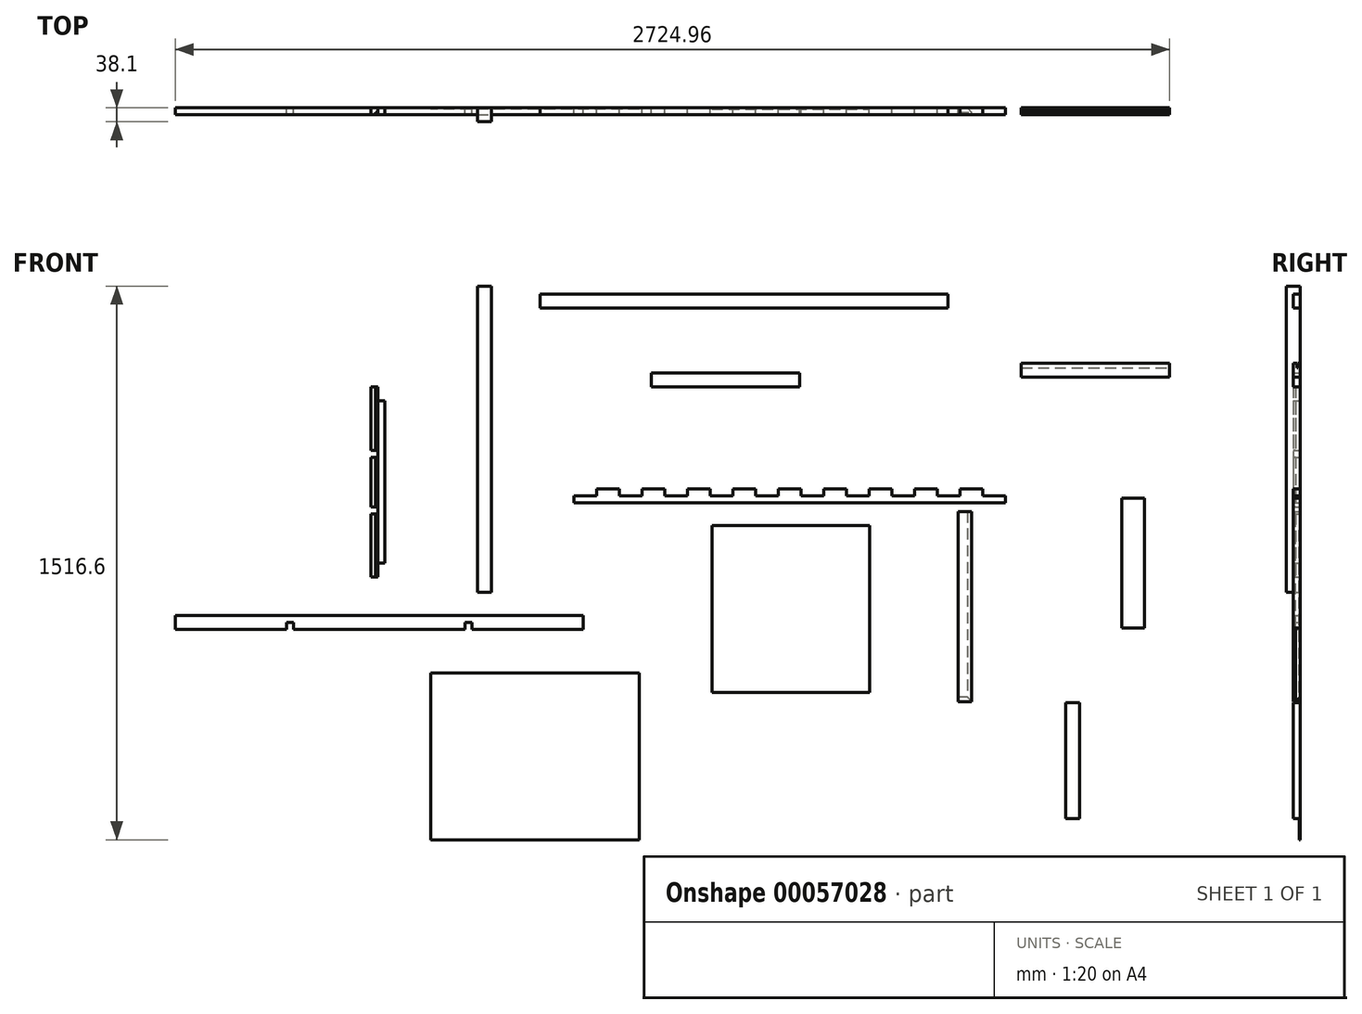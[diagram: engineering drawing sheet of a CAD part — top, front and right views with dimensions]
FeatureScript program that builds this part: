
annotation { "Feature Type Name" : "Feature", "Feature Type Description" : "" }
export const myFeature = defineFeature(function(context is Context, id is Id, definition is map)
    precondition{}
    {
        {
            var Q0;
            Q0=qCreatedBy(makeId("Front.planeOp"),FACE);
            var sketch = newSketch(context, id + "F0", { "sketchPlane" : qUnion([Q0])});
            skLineSegment(sketch, "E0.bottom", {"start": v(-712.43, -105.84) * mm, "end": v(-650.2, -105.84) * mm});
            skLineSegment(sketch, "E0.left", {"start": v(-774.66, -124.9) * mm, "end": v(-774.66, -143.94) * mm});
            skPoint(sketch, "E1.oppositeSnap0", {"position": v(-876.9, -124.9) * mm});
            skLineSegment(sketch, "E1.top", {"start": v(-774.66, -124.9) * mm, "end": v(-712.43, -124.9) * mm});
            skLineSegment(sketch, "E1.right", {"start": v(-712.43, -105.84) * mm, "end": v(-712.43, -124.9) * mm});
            skLineSegment(sketch, "E2.top", {"start": v(-650.2, -124.9) * mm, "end": v(-587.97, -124.9) * mm});
            skLineSegment(sketch, "E2.left", {"start": v(-650.2, -105.84) * mm, "end": v(-650.2, -124.9) * mm});
            skLineSegment(sketch, "E2.right", {"start": v(-587.97, -105.84) * mm, "end": v(-587.97, -124.9) * mm});
            skLineSegment(sketch, "E3.top", {"start": v(-525.74, -124.9) * mm, "end": v(-463.51, -124.9) * mm});
            skLineSegment(sketch, "E3.left", {"start": v(-525.74, -105.84) * mm, "end": v(-525.74, -124.9) * mm});
            skLineSegment(sketch, "E3.right", {"start": v(-463.51, -105.84) * mm, "end": v(-463.51, -124.9) * mm});
            skLineSegment(sketch, "E4.top", {"start": v(-401.28, -124.9) * mm, "end": v(-339.05, -124.9) * mm});
            skLineSegment(sketch, "E4.left", {"start": v(-401.28, -105.84) * mm, "end": v(-401.28, -124.9) * mm});
            skLineSegment(sketch, "E4.right", {"start": v(-339.05, -105.84) * mm, "end": v(-339.05, -124.9) * mm});
            skLineSegment(sketch, "E5.top", {"start": v(-276.82, -124.9) * mm, "end": v(-214.6, -124.9) * mm});
            skLineSegment(sketch, "E5.left", {"start": v(-276.82, -105.84) * mm, "end": v(-276.82, -124.9) * mm});
            skLineSegment(sketch, "E5.right", {"start": v(-214.6, -105.84) * mm, "end": v(-214.6, -124.9) * mm});
            skLineSegment(sketch, "E6.top", {"start": v(-152.36, -124.9) * mm, "end": v(-90.13, -124.9) * mm});
            skLineSegment(sketch, "E6.left", {"start": v(-152.36, -105.84) * mm, "end": v(-152.36, -124.9) * mm});
            skLineSegment(sketch, "E6.right", {"start": v(-90.13, -105.84) * mm, "end": v(-90.13, -124.9) * mm});
            skLineSegment(sketch, "E7.top", {"start": v(-27.9, -124.9) * mm, "end": v(34.33, -124.9) * mm});
            skLineSegment(sketch, "E7.left", {"start": v(-27.9, -105.84) * mm, "end": v(-27.9, -124.9) * mm});
            skLineSegment(sketch, "E7.right", {"start": v(34.33, -105.84) * mm, "end": v(34.33, -124.9) * mm});
            skLineSegment(sketch, "E8.top", {"start": v(96.56, -124.9) * mm, "end": v(158.79, -124.9) * mm});
            skLineSegment(sketch, "E8.left", {"start": v(96.56, -105.84) * mm, "end": v(96.56, -124.9) * mm});
            skLineSegment(sketch, "E8.right", {"start": v(158.79, -105.84) * mm, "end": v(158.79, -124.9) * mm});
            skPoint(sketch, "E9.orphan", {"position": v(-774.66, -105.84) * mm});
            skLineSegment(sketch, "E10.trimOffspring", {"start": v(-463.51, -105.84) * mm, "end": v(-401.28, -105.84) * mm});
            skLineSegment(sketch, "E11.trimOffspring", {"start": v(-587.97, -105.84) * mm, "end": v(-525.74, -105.84) * mm});
            skLineSegment(sketch, "E12.trimOffspring", {"start": v(-339.05, -105.84) * mm, "end": v(-276.82, -105.84) * mm});
            skLineSegment(sketch, "E13.trimOffspring", {"start": v(-214.6, -105.84) * mm, "end": v(-152.36, -105.84) * mm});
            skLineSegment(sketch, "E14.trimOffspring", {"start": v(-90.13, -105.84) * mm, "end": v(-27.9, -105.84) * mm});
            skLineSegment(sketch, "E15.trimOffspring", {"start": v(34.33, -105.84) * mm, "end": v(96.56, -105.84) * mm});
            skLineSegment(sketch, "E16.trimOffspring", {"start": v(158.79, -105.84) * mm, "end": v(221.02, -105.84) * mm});
            skLineSegment(sketch, "E17.top", {"start": v(221.02, -124.9) * mm, "end": v(283.25, -124.9) * mm});
            skLineSegment(sketch, "E17.left", {"start": v(221.02, -105.84) * mm, "end": v(221.02, -124.9) * mm});
            skLineSegment(sketch, "E17.right", {"start": v(283.25, -105.84) * mm, "end": v(283.25, -124.9) * mm});
            skLineSegment(sketch, "E18.top", {"start": v(345.48, -124.9) * mm, "end": v(407.7, -124.9) * mm});
            skLineSegment(sketch, "E18.left", {"start": v(345.48, -105.84) * mm, "end": v(345.48, -124.9) * mm});
            skLineSegment(sketch, "E19.trimOffspring", {"start": v(283.25, -105.84) * mm, "end": v(345.48, -105.84) * mm});
            skLineSegment(sketch, "E20", {"start": v(-774.66, -143.94) * mm, "end": v(407.43, -143.94) * mm});
            skLineSegment(sketch, "E21", {"start": v(407.43, -143.94) * mm, "end": v(407.7, -124.9) * mm});
            skSolve(sketch);
        }
        {
            var Q0;
            Q0 = qSketchRegion(id + "F0", true);
            extrude(context, id + "F1", {"entities" : qUnion([Q0]), "depth" : 19.05 * mm});
        }
        {
            var Q0;
            Q0=qCreatedBy(makeId("Front.planeOp"),FACE);
            var sketch = newSketch(context, id + "F2", { "sketchPlane" : qUnion([Q0])});
            skLineSegment(sketch, "E22.bottom", {"start": v(-1039.05, 450.08) * mm, "end": v(-1000.95, 450.08) * mm});
            skLineSegment(sketch, "E22.top", {"start": v(-1039.05, -388.12) * mm, "end": v(-1000.95, -388.12) * mm});
            skLineSegment(sketch, "E22.left", {"start": v(-1039.05, 450.08) * mm, "end": v(-1039.05, -388.12) * mm});
            skLineSegment(sketch, "E22.right", {"start": v(-1000.95, 450.08) * mm, "end": v(-1000.95, -388.12) * mm});
            skSolve(sketch);
        }
        {
            var Q0;
            Q0 = qSketchRegion(id + "F2", true);
            extrude(context, id + "F3", {"entities" : qUnion([Q0]), "depth" : 38.1 * mm});
        }
        {
            var Q0;
            Q0=qCreatedBy(makeId("Front.planeOp"),FACE);
            var sketch = newSketch(context, id + "F4", { "sketchPlane" : qUnion([Q0])});
            skLineSegment(sketch, "E23.bottom", {"start": v(-867.04, 428.45) * mm, "end": v(250.56, 428.45) * mm});
            skLineSegment(sketch, "E23.top", {"start": v(-867.04, 390.35) * mm, "end": v(250.56, 390.35) * mm});
            skLineSegment(sketch, "E23.left", {"start": v(-867.04, 428.45) * mm, "end": v(-867.04, 390.35) * mm});
            skLineSegment(sketch, "E23.right", {"start": v(250.56, 428.45) * mm, "end": v(250.56, 390.35) * mm});
            skSolve(sketch);
        }
        {
            var Q0;
            Q0 = qSketchRegion(id + "F4", true);
            extrude(context, id + "F5", {"entities" : qUnion([Q0]), "depth" : 19.05 * mm});
        }
        {
            var Q0;
            Q0=qCreatedBy(makeId("Front.planeOp"),FACE);
            var sketch = newSketch(context, id + "F6", { "sketchPlane" : qUnion([Q0])});
            skLineSegment(sketch, "E24.bottom", {"start": v(451.47, 239.2) * mm, "end": v(857.87, 239.2) * mm});
            skLineSegment(sketch, "E24.top", {"start": v(451.47, 201.1) * mm, "end": v(857.87, 201.1) * mm});
            skLineSegment(sketch, "E24.left", {"start": v(451.47, 239.2) * mm, "end": v(451.47, 201.1) * mm});
            skLineSegment(sketch, "E24.right", {"start": v(857.87, 239.2) * mm, "end": v(857.87, 201.1) * mm});
            skSolve(sketch);
        }
        {
            var Q0;
            Q0 = qSketchRegion(id + "F6", true);
            extrude(context, id + "F7", {"entities" : qUnion([Q0]), "depth" : 19.05 * mm});
        }
        {
            var Q0;
            Q0=qCreatedBy(makeId("Front.planeOp"),FACE);
            var sketch = newSketch(context, id + "F8", { "sketchPlane" : qUnion([Q0])});
            skLineSegment(sketch, "E25.bottom", {"start": v(726.67, -130.46) * mm, "end": v(788.9, -130.46) * mm});
            skLineSegment(sketch, "E25.top", {"start": v(726.67, -486.06) * mm, "end": v(788.9, -486.06) * mm});
            skLineSegment(sketch, "E25.left", {"start": v(726.67, -130.46) * mm, "end": v(726.67, -486.06) * mm});
            skLineSegment(sketch, "E25.right", {"start": v(788.9, -130.46) * mm, "end": v(788.9, -486.06) * mm});
            skSolve(sketch);
        }
        {
            var Q0;
            Q0 = qSketchRegion(id + "F8", true);
            extrude(context, id + "F9", {"entities" : qUnion([Q0]), "depth" : 19.05 * mm});
        }
        {
            var Q0;
            Q0=qCreatedBy(makeId("Front.planeOp"),FACE);
            var sketch = newSketch(context, id + "F10", { "sketchPlane" : qUnion([Q0])});
            skLineSegment(sketch, "E26.bottom", {"start": v(-396.53, -662.46) * mm, "end": v(35.27, -662.46) * mm});
            skLineSegment(sketch, "E26.top", {"start": v(-396.53, -205.26) * mm, "end": v(35.27, -205.26) * mm});
            skLineSegment(sketch, "E26.left", {"start": v(-396.53, -662.46) * mm, "end": v(-396.53, -205.26) * mm});
            skLineSegment(sketch, "E26.right", {"start": v(35.27, -662.46) * mm, "end": v(35.27, -205.26) * mm});
            skSolve(sketch);
        }
        {
            var Q0;
            Q0 = qSketchRegion(id + "F10", true);
            extrude(context, id + "F11", {"entities" : qUnion([Q0]), "depth" : 3.17 * mm});
        }
        {
            var Q0;
            Q0=makeQuery(id+"F7.opExtrude","SWEPT_FACE",FACE,{"disambiguationData":[OSD([sQuery(id+"F6.wireOp",EDGE,"E24.bottom")])]});
            var sketch = newSketch(context, id + "F12", { "sketchPlane" : qUnion([Q0])});
            skLineSegment(sketch, "E27.bottom", {"start": v(451.47, -6.35) * mm, "end": v(857.87, -6.35) * mm});
            skLineSegment(sketch, "E27.top", {"start": v(451.47, -9.53) * mm, "end": v(857.87, -9.53) * mm});
            skLineSegment(sketch, "E27.left", {"start": v(451.47, -6.35) * mm, "end": v(451.47, -9.53) * mm});
            skLineSegment(sketch, "E27.right", {"start": v(857.87, -6.35) * mm, "end": v(857.87, -9.53) * mm});
            skSolve(sketch);
        }
        {
            var Q0;
            Q0 = qSketchRegion(id + "F12", true);
            extrude(context, id + "F13", {"entities" : qUnion([Q0]), "operationType" : NewBodyOperationType.REMOVE, "oppositeDirection" : true, "depth" : 12.7 * mm});
        }
        {
            var Q0;
            Q0=qCreatedBy(makeId("Front.planeOp"),FACE);
            var sketch = newSketch(context, id + "F14", { "sketchPlane" : qUnion([Q0])});
            skLineSegment(sketch, "E28.bottom", {"start": v(-1330.52, 135.47) * mm, "end": v(-1292.42, 135.47) * mm});
            skLineSegment(sketch, "E28.top", {"start": v(-1330.52, -309.03) * mm, "end": v(-1292.42, -309.03) * mm});
            skLineSegment(sketch, "E28.left", {"start": v(-1330.52, 135.47) * mm, "end": v(-1330.52, 0) * mm});
            skLineSegment(sketch, "E28.right", {"start": v(-1292.42, 135.47) * mm, "end": v(-1292.42, -309.03) * mm});
            skLineSegment(sketch, "E29.bottom", {"start": v(-1330.52, 0) * mm, "end": v(-1311.47, 0) * mm});
            skLineSegment(sketch, "E29.top", {"start": v(-1330.52, -19.05) * mm, "end": v(-1311.47, -19.05) * mm});
            skLineSegment(sketch, "E29.right", {"start": v(-1311.47, 0) * mm, "end": v(-1311.47, -19.05) * mm});
            skLineSegment(sketch, "E30.bottom", {"start": v(-1330.52, -173.57) * mm, "end": v(-1311.47, -173.57) * mm});
            skLineSegment(sketch, "E30.top", {"start": v(-1330.52, -154.52) * mm, "end": v(-1311.47, -154.52) * mm});
            skLineSegment(sketch, "E30.right", {"start": v(-1311.47, -173.57) * mm, "end": v(-1311.47, -154.52) * mm});
            skLineSegment(sketch, "E31.trimOffspring", {"start": v(-1330.52, -19.05) * mm, "end": v(-1330.52, -154.52) * mm});
            skLineSegment(sketch, "E32.trimOffspring", {"start": v(-1330.52, -173.57) * mm, "end": v(-1330.52, -309.03) * mm});
            skLineSegment(sketch, "E33.bottom", {"start": v(-1330.52, 135.47) * mm, "end": v(-1279.72, 135.47) * mm});
            skLineSegment(sketch, "E34.bottom", {"start": v(-1330.52, -309.03) * mm, "end": v(-1279.72, -309.03) * mm});
            skLineSegment(sketch, "E35.bottom", {"start": v(-1330.52, 135.47) * mm, "end": v(-1311.47, 135.47) * mm});
            skLineSegment(sketch, "E35.top", {"start": v(-1330.52, 173.57) * mm, "end": v(-1311.47, 173.57) * mm});
            skLineSegment(sketch, "E35.left", {"start": v(-1330.52, 135.47) * mm, "end": v(-1330.52, 173.57) * mm});
            skLineSegment(sketch, "E35.right", {"start": v(-1311.47, 135.47) * mm, "end": v(-1311.47, 173.57) * mm});
            skLineSegment(sketch, "E36.bottom", {"start": v(-1330.52, -309.03) * mm, "end": v(-1311.47, -309.03) * mm});
            skLineSegment(sketch, "E36.top", {"start": v(-1330.52, -347.13) * mm, "end": v(-1311.47, -347.13) * mm});
            skLineSegment(sketch, "E36.left", {"start": v(-1330.52, -309.03) * mm, "end": v(-1330.52, -347.13) * mm});
            skLineSegment(sketch, "E36.right", {"start": v(-1311.47, -309.03) * mm, "end": v(-1311.47, -347.13) * mm});
            skSolve(sketch);
        }
        {
            var Q0;
            Q0 = qSketchRegion(id + "F14", true);
            extrude(context, id + "F15", {"entities" : qUnion([Q0]), "depth" : 19.05 * mm});
        }
        {
            var Q0;
            Q0=qCreatedBy(makeId("Front.planeOp"),FACE);
            var sketch = newSketch(context, id + "F16", { "sketchPlane" : qUnion([Q0])});
            skLineSegment(sketch, "E37.bottom", {"start": v(-1867.09, -452.1) * mm, "end": v(-749.49, -452.1) * mm});
            skLineSegment(sketch, "E37.top", {"start": v(-1867.09, -490.2) * mm, "end": v(-1562.29, -490.2) * mm});
            skLineSegment(sketch, "E37.left", {"start": v(-1867.09, -452.1) * mm, "end": v(-1867.09, -490.2) * mm});
            skLineSegment(sketch, "E37.right", {"start": v(-749.49, -452.1) * mm, "end": v(-749.49, -490.2) * mm});
            skLineSegment(sketch, "E38.top", {"start": v(-1562.29, -471.16) * mm, "end": v(-1543.24, -471.16) * mm});
            skLineSegment(sketch, "E38.left", {"start": v(-1562.29, -490.2) * mm, "end": v(-1562.29, -471.16) * mm});
            skLineSegment(sketch, "E38.right", {"start": v(-1543.24, -490.2) * mm, "end": v(-1543.24, -471.16) * mm});
            skLineSegment(sketch, "E39.top", {"start": v(-1073.34, -471.16) * mm, "end": v(-1054.29, -471.16) * mm});
            skLineSegment(sketch, "E39.left", {"start": v(-1073.34, -490.2) * mm, "end": v(-1073.34, -471.16) * mm});
            skLineSegment(sketch, "E39.right", {"start": v(-1054.29, -490.2) * mm, "end": v(-1054.29, -471.16) * mm});
            skLineSegment(sketch, "E40.trimOffspring", {"start": v(-1543.24, -490.2) * mm, "end": v(-1073.34, -490.2) * mm});
            skLineSegment(sketch, "E41.trimOffspring", {"start": v(-1054.29, -490.2) * mm, "end": v(-749.49, -490.2) * mm});
            skSolve(sketch);
        }
        {
            var Q0;
            Q0 = qSketchRegion(id + "F16", true);
            extrude(context, id + "F17", {"entities" : qUnion([Q0]), "depth" : 19.05 * mm});
        }
        {
            var Q0;
            Q0=qCreatedBy(makeId("Front.planeOp"),FACE);
            var sketch = newSketch(context, id + "F18", { "sketchPlane" : qUnion([Q0])});
            skLineSegment(sketch, "E42.bottom", {"start": v(-561.82, 212.25) * mm, "end": v(-155.42, 212.25) * mm});
            skLineSegment(sketch, "E42.top", {"start": v(-561.82, 174.15) * mm, "end": v(-155.42, 174.15) * mm});
            skLineSegment(sketch, "E42.left", {"start": v(-561.82, 212.25) * mm, "end": v(-561.82, 174.15) * mm});
            skLineSegment(sketch, "E42.right", {"start": v(-155.42, 212.25) * mm, "end": v(-155.42, 174.15) * mm});
            skSolve(sketch);
        }
        {
            var Q0;
            Q0 = qSketchRegion(id + "F18", true);
            extrude(context, id + "F19", {"entities" : qUnion([Q0]), "depth" : 19.05 * mm});
        }
        {
            var Q0;
            Q0=qCreatedBy(makeId("Front.planeOp"),FACE);
            var sketch = newSketch(context, id + "F20", { "sketchPlane" : qUnion([Q0])});
            skLineSegment(sketch, "E43.bottom", {"start": v(277.75, -167.96) * mm, "end": v(315.85, -167.96) * mm});
            skLineSegment(sketch, "E43.top", {"start": v(277.75, -688.66) * mm, "end": v(315.85, -688.66) * mm});
            skLineSegment(sketch, "E43.left", {"start": v(277.75, -167.96) * mm, "end": v(277.75, -688.66) * mm});
            skLineSegment(sketch, "E43.right", {"start": v(315.85, -167.96) * mm, "end": v(315.85, -688.66) * mm});
            skSolve(sketch);
        }
        {
            var Q0;
            Q0 = qSketchRegion(id + "F20", true);
            extrude(context, id + "F21", {"entities" : qUnion([Q0]), "depth" : 19.05 * mm});
        }
        {
            var Q0;
            Q0=makeQuery(id+"F21.opExtrude","CAP_EDGE",EDGE,{"disambiguationData":[OSD([sQuery(id+"F20.wireOp",EDGE,"E43.top")])],"isStart":true});
            chamfer(context, id + "F22", {"entities" : qUnion([Q0]), "width" : 12.7 * mm, "tangentPropagation" : true});
        }
        {
            var Q0;
            Q0=makeQuery(id+"F21.opExtrude","CAP_EDGE",EDGE,{"disambiguationData":[OSD([sQuery(id+"F20.wireOp",EDGE,"E43.right")])],"isStart":true});
            chamfer(context, id + "F23", {"entities" : qUnion([Q0]), "width" : 12.7 * mm, "tangentPropagation" : true});
        }
        {
            var Q0;
            Q0=qCreatedBy(makeId("Front.planeOp"),FACE);
            var sketch = newSketch(context, id + "F24", { "sketchPlane" : qUnion([Q0])});
            skLineSegment(sketch, "E44.bottom", {"start": v(-595.59, -609.32) * mm, "end": v(-1167.09, -609.32) * mm});
            skLineSegment(sketch, "E44.top", {"start": v(-595.59, -1066.52) * mm, "end": v(-1167.09, -1066.52) * mm});
            skLineSegment(sketch, "E44.left", {"start": v(-595.59, -609.32) * mm, "end": v(-595.59, -1066.52) * mm});
            skLineSegment(sketch, "E44.right", {"start": v(-1167.09, -609.32) * mm, "end": v(-1167.09, -1066.52) * mm});
            skSolve(sketch);
        }
        {
            var Q0;
            Q0 = qSketchRegion(id + "F24", true);
            extrude(context, id + "F25", {"entities" : qUnion([Q0]), "depth" : 3.17 * mm});
        }
        {
            var Q0;
            Q0=qCreatedBy(makeId("Front.planeOp"),FACE);
            var sketch = newSketch(context, id + "F26", { "sketchPlane" : qUnion([Q0])});
            skLineSegment(sketch, "E45.bottom", {"start": v(611.47, -691.34) * mm, "end": v(573.37, -691.34) * mm});
            skLineSegment(sketch, "E45.top", {"start": v(611.47, -1008.84) * mm, "end": v(573.37, -1008.84) * mm});
            skLineSegment(sketch, "E45.left", {"start": v(611.47, -691.34) * mm, "end": v(611.47, -1008.84) * mm});
            skLineSegment(sketch, "E45.right", {"start": v(573.37, -691.34) * mm, "end": v(573.37, -1008.84) * mm});
            skSolve(sketch);
        }
        {
            var Q0;
            Q0 = qSketchRegion(id + "F26", true);
            extrude(context, id + "F27", {"entities" : qUnion([Q0]), "depth" : 19.05 * mm});
        }
        {
            var Q0;
            Q0=makeQuery(id+"F15.opExtrude","CAP_FACE",FACE,{"disambiguationData":[OSD([sQuery(id+"F14.wireOp",EDGE,"E28.left"),sQuery(id+"F14.wireOp",EDGE,"E28.right"),sQuery(id+"F14.wireOp",EDGE,"E29.bottom"),sQuery(id+"F14.wireOp",EDGE,"E29.top"),sQuery(id+"F14.wireOp",EDGE,"E29.right"),sQuery(id+"F14.wireOp",EDGE,"E30.bottom"),sQuery(id+"F14.wireOp",EDGE,"E30.top"),sQuery(id+"F14.wireOp",EDGE,"E30.right"),sQuery(id+"F14.wireOp",EDGE,"E31.trimOffspring"),sQuery(id+"F14.wireOp",EDGE,"E32.trimOffspring"),sQuery(id+"F14.wireOp",EDGE,"E33.bottom"),sQuery(id+"F14.wireOp",EDGE,"E34.bottom"),sQuery(id+"F14.wireOp",EDGE,"E35.top"),sQuery(id+"F14.wireOp",EDGE,"E35.left"),sQuery(id+"F14.wireOp",EDGE,"E35.right"),sQuery(id+"F14.wireOp",EDGE,"E36.top"),sQuery(id+"F14.wireOp",EDGE,"E36.left"),sQuery(id+"F14.wireOp",EDGE,"E36.right")])],"isStart":false});
            var sketch = newSketch(context, id + "F28", { "sketchPlane" : qUnion([Q0])});
            skLineSegment(sketch, "E46.bottom", {"start": v(-1317.82, 173.57) * mm, "end": v(-1311.47, 173.57) * mm});
            skLineSegment(sketch, "E46.top", {"start": v(-1317.82, -347.13) * mm, "end": v(-1311.47, -347.13) * mm});
            skLineSegment(sketch, "E46.left", {"start": v(-1317.82, 173.57) * mm, "end": v(-1317.82, -347.13) * mm});
            skLineSegment(sketch, "E46.right", {"start": v(-1311.47, 173.57) * mm, "end": v(-1311.47, -347.13) * mm});
            skSolve(sketch);
        }
        {
            var Q0;
            Q0 = qSketchRegion(id + "F28", true);
            extrude(context, id + "F29", {"entities" : qUnion([Q0]), "operationType" : NewBodyOperationType.REMOVE, "oppositeDirection" : true, "depth" : 6.35 * mm});
        }
    });
